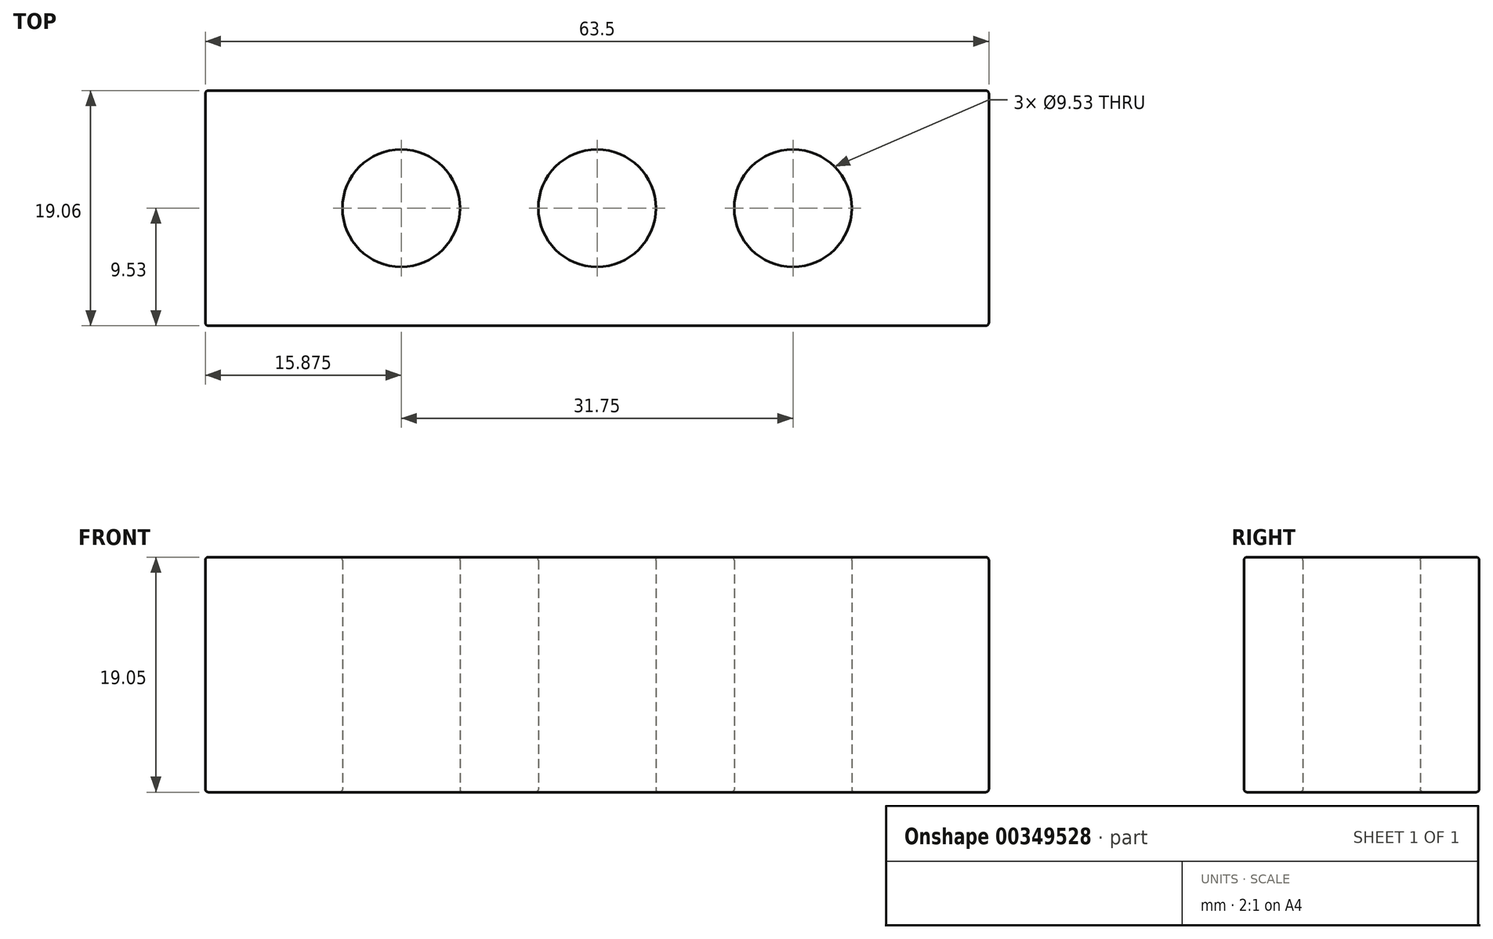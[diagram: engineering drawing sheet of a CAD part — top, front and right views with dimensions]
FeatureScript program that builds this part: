
annotation { "Feature Type Name" : "Feature", "Feature Type Description" : "" }
export const myFeature = defineFeature(function(context is Context, id is Id, definition is map)
    precondition{}
    {
        {
            var Q0;
            Q0=qCreatedBy(makeId("Front.planeOp"),FACE);
            var sketch = newSketch(context, id + "F0", { "sketchPlane" : qUnion([Q0])});
            skLineSegment(sketch, "E0.bottom", {"start": v(31.75, 9.53) * mm, "end": v(-31.75, 9.53) * mm});
            skLineSegment(sketch, "E0.top", {"start": v(31.75, -9.53) * mm, "end": v(-31.75, -9.53) * mm});
            skLineSegment(sketch, "E0.left", {"start": v(31.75, 9.53) * mm, "end": v(31.75, -9.53) * mm});
            skLineSegment(sketch, "E0.right", {"start": v(-31.75, 9.53) * mm, "end": v(-31.75, -9.53) * mm});
            skPoint(sketch, "E0.middle", {"position": v(0, 0) * mm});
            skCircle(sketch, "E1", {"center": v(0, 0) * mm, "radius": 4.76 * mm});
            skLineSegment(sketch, "E2", {"start": v(0, 0) * mm, "end": v(15.88, 0) * mm, "construction": true});
            skCircle(sketch, "E3", {"center": v(15.88, 0) * mm, "radius": 4.76 * mm});
            skCircle(sketch, "E4.MirrorC", {"center": v(-15.88, 0) * mm, "radius": 4.76 * mm});
            skSolve(sketch);
        }
        {
            var Q0;
            Q0 = qSketchRegion(id + "F0", true);
            extrude(context, id + "F1", {"entities" : qUnion([Q0]), "oppositeDirection" : true, "depth" : 19.05 * mm});
        }
        {
            var Q0;
            Q0=qCreatedBy(makeId("Front.planeOp"),FACE);
            var sketch = newSketch(context, id + "F2", { "sketchPlane" : qUnion([Q0])});
            skLineSegment(sketch, "E5.bottom", {"start": v(4.76, 4.76) * mm, "end": v(-4.76, 4.76) * mm});
            skLineSegment(sketch, "E5.top", {"start": v(4.76, -4.76) * mm, "end": v(-4.76, -4.76) * mm});
            skLineSegment(sketch, "E5.left", {"start": v(4.76, 4.76) * mm, "end": v(4.76, -4.76) * mm});
            skLineSegment(sketch, "E5.right", {"start": v(-4.76, 4.76) * mm, "end": v(-4.76, -4.76) * mm});
            skPoint(sketch, "E5.middle", {"position": v(0, 0) * mm});
            skLineSegment(sketch, "E6.bottom", {"start": v(-11.11, 4.76) * mm, "end": v(-20.64, 4.76) * mm});
            skLineSegment(sketch, "E6.top", {"start": v(-11.11, -4.76) * mm, "end": v(-20.64, -4.76) * mm});
            skLineSegment(sketch, "E6.left", {"start": v(-11.11, 4.76) * mm, "end": v(-11.11, -4.76) * mm});
            skLineSegment(sketch, "E6.right", {"start": v(-20.64, 4.76) * mm, "end": v(-20.64, -4.76) * mm});
            skPoint(sketch, "E6.middle", {"position": v(-15.88, 0) * mm});
            skLineSegment(sketch, "E7.MirrorCS", {"start": v(20.64, 4.76) * mm, "end": v(20.64, -4.76) * mm});
            skLineSegment(sketch, "E8.MirrorCS", {"start": v(11.11, 4.76) * mm, "end": v(20.64, 4.76) * mm});
            skPoint(sketch, "E9.MirrorP", {"position": v(15.88, 0) * mm});
            skLineSegment(sketch, "E10.MirrorCS", {"start": v(11.11, -4.76) * mm, "end": v(20.64, -4.76) * mm});
            skLineSegment(sketch, "E11.MirrorCS", {"start": v(11.11, 4.76) * mm, "end": v(11.11, -4.76) * mm});
            skSolve(sketch);
        }
        {
            var Q0;
            Q0=makeQuery(id+"F1.opExtrude","CAP_FACE",FACE,{"disambiguationData":[OSD([sQuery(id+"F0.wireOp",EDGE,"E0.bottom"),sQuery(id+"F0.wireOp",EDGE,"E0.top"),sQuery(id+"F0.wireOp",EDGE,"E0.left"),sQuery(id+"F0.wireOp",EDGE,"E0.right"),sQuery(id+"F0.wireOp",EDGE,"E1"),sQuery(id+"F0.wireOp",EDGE,"E3"),sQuery(id+"F0.wireOp",EDGE,"E4.MirrorC")])],"isStart":false});
            var Q1;
            Q1=makeQuery(id+"F1.opExtrude","CAP_FACE",FACE,{"disambiguationData":[OSD([sQuery(id+"F0.wireOp",EDGE,"E0.bottom"),sQuery(id+"F0.wireOp",EDGE,"E0.top"),sQuery(id+"F0.wireOp",EDGE,"E0.left"),sQuery(id+"F0.wireOp",EDGE,"E0.right"),sQuery(id+"F0.wireOp",EDGE,"E1"),sQuery(id+"F0.wireOp",EDGE,"E3"),sQuery(id+"F0.wireOp",EDGE,"E4.MirrorC")])],"isStart":true});
            var Q2;
            Q2=makeQuery(id+"F1.opExtrude","SWEPT_FACE",FACE,{"disambiguationData":[OSD([sQuery(id+"F0.wireOp",EDGE,"E0.left")])]});
            var Q3;
            Q3=makeQuery(id+"F1.opExtrude","SWEPT_FACE",FACE,{"disambiguationData":[OSD([sQuery(id+"F0.wireOp",EDGE,"E0.right")])]});
            fillet(context, id + "F3", {"entities" : qUnion([Q0, Q1, Q2, Q3]), "radius" : 0.25 * mm, "tangentPropagation" : true, "allowEdgeOverflow" : false});
        }
        {
            var Q0;
            Q0=makeQuery(id+"F1.opExtrude","SWEPT_BODY",BODY,{"disambiguationData":[OSD([sQuery(id+"F0.wireOp",EDGE,"E0.bottom"),sQuery(id+"F0.wireOp",EDGE,"E0.top"),sQuery(id+"F0.wireOp",EDGE,"E0.left"),sQuery(id+"F0.wireOp",EDGE,"E0.right"),sQuery(id+"F0.wireOp",EDGE,"E1"),sQuery(id+"F0.wireOp",EDGE,"E3"),sQuery(id+"F0.wireOp",EDGE,"E4.MirrorC")])]});
            var Q1;
            Q1=sQuery(id+"F0.wireOp",EDGE,"E2");
            transform(context, id + "F4", {"entities" : qUnion([Q0]), "transformType" : TransformType.ROTATION, "transformAxis" : qUnion([Q1]), "angle" : 90 * degree, "makeCopy" : false});
        }
    });
